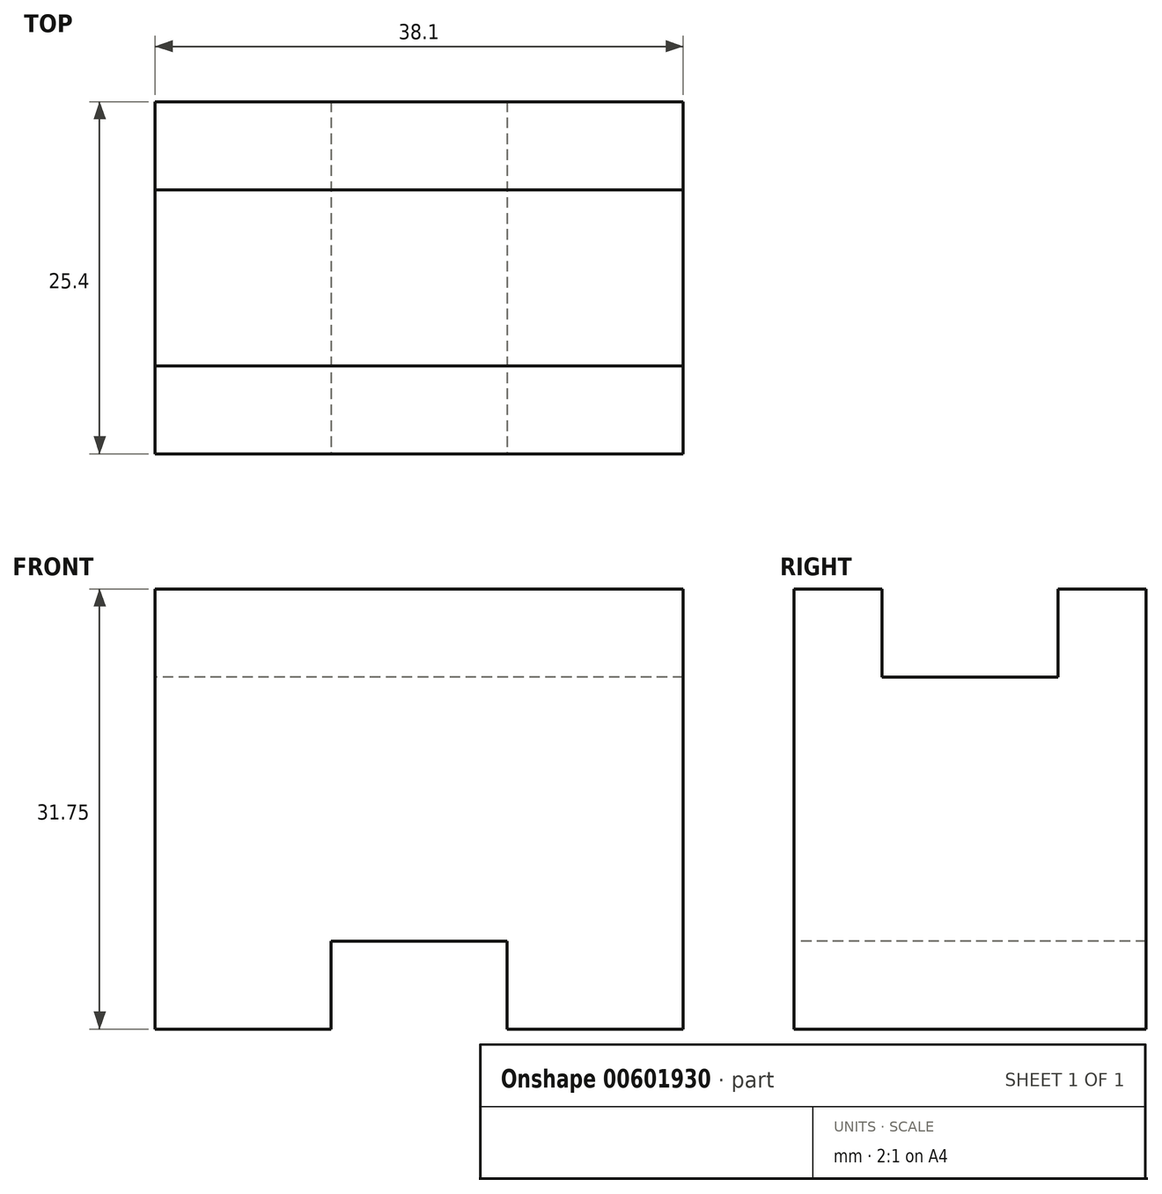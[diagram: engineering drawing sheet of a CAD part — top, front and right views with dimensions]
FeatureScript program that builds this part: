
annotation { "Feature Type Name" : "Feature", "Feature Type Description" : "" }
export const myFeature = defineFeature(function(context is Context, id is Id, definition is map)
    precondition{}
    {
        {
            var Q0;
            Q0=qCreatedBy(makeId("Right.planeOp"),FACE);
            var sketch = newSketch(context, id + "F0", { "sketchPlane" : qUnion([Q0])});
            skLineSegment(sketch, "E0", {"start": v(0, 0) * mm, "end": v(0, 31.75) * mm});
            skLineSegment(sketch, "E1", {"start": v(0, 31.75) * mm, "end": v(6.35, 31.75) * mm});
            skLineSegment(sketch, "E2", {"start": v(6.35, 31.75) * mm, "end": v(6.35, 25.4) * mm});
            skLineSegment(sketch, "E3", {"start": v(6.35, 25.4) * mm, "end": v(19.05, 25.4) * mm});
            skLineSegment(sketch, "E4", {"start": v(19.05, 25.4) * mm, "end": v(19.05, 31.75) * mm});
            skLineSegment(sketch, "E5", {"start": v(19.05, 31.75) * mm, "end": v(25.4, 31.75) * mm});
            skLineSegment(sketch, "E6", {"start": v(25.4, 31.75) * mm, "end": v(25.4, 0) * mm});
            skLineSegment(sketch, "E7", {"start": v(0, 0) * mm, "end": v(25.4, 0) * mm});
            skSolve(sketch);
        }
        {
            var Q0;
            Q0=makeQuery(id+"F0.imprint","IMPRINT",FACE,{"disambiguationData":[TD([[makeQuery(id+"F0.imprint","IMPRINT",EDGE,{"derivedFrom":sQuery(id+"F0.wireOp",EDGE,"E0")}),-1.0]])]});
            extrude(context, id + "F1", {"entities" : qUnion([Q0]), "depth" : 38.1 * mm, "offsetDistance" : 25.4 * mm});
        }
        {
            var Q0;
            Q0=makeQuery(id+"F1.opExtrude","SWEPT_FACE",FACE,{"disambiguationData":[OSD([sQuery(id+"F0.wireOp",EDGE,"E0")])]});
            var sketch = newSketch(context, id + "F2", { "sketchPlane" : qUnion([Q0])});
            skLineSegment(sketch, "E8", {"start": v(0, 0) * mm, "end": v(12.7, 0) * mm});
            skLineSegment(sketch, "E9", {"start": v(38.1, 0) * mm, "end": v(25.4, 0) * mm});
            skLineSegment(sketch, "E10", {"start": v(12.7, 0) * mm, "end": v(12.7, 6.35) * mm});
            skLineSegment(sketch, "E11", {"start": v(25.4, 0) * mm, "end": v(25.4, 6.35) * mm});
            skLineSegment(sketch, "E12", {"start": v(12.7, 6.35) * mm, "end": v(25.4, 6.35) * mm});
            skSolve(sketch);
        }
        {
            var Q0;
            Q0=makeQuery(id+"F2.imprint","IMPRINT",FACE,{"disambiguationData":[TD([[makeQuery(id+"F2.imprint","IMPRINT",EDGE,{"derivedFrom":sQuery(id+"F2.wireOp",EDGE,"E8")}),-1.0]])]});
            var sketch = newSketch(context, id + "F3", { "sketchPlane" : qUnion([Q0])});
            skLineSegment(sketch, "E13", {"start": v(12.68, 0) * mm, "end": v(25.38, 0) * mm});
            skSolve(sketch);
        }
        {
            var Q0;
            Q0 = qSketchRegion(id + "F3", true);
            var Q1;
            {var subQ0=sQuery(id+"F2.wireOp",EDGE,"E10");Q1=makeQuery(id+"F2.imprint","IMPRINT",FACE,{"disambiguationData":[TD([[makeQuery(id+"F2.imprint","IMPRINT",EDGE,{"derivedFrom":subQ0}),-1.0]])]});}
            extrude(context, id + "F4", {"entities" : qUnion([Q0, Q1]), "operationType" : NewBodyOperationType.REMOVE, "oppositeDirection" : true, "depth" : 25.4 * mm, "offsetDistance" : 25.4 * mm});
        }
    });
